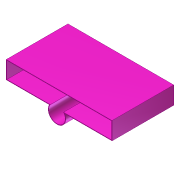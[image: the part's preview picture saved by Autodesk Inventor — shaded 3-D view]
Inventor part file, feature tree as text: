
AUTODESK INVENTOR PART (.ipt)
format: ipt  version: 2012 (Build 160160000, 160)  size: 87,552 bytes
history: native  units: in
note: dims shown in document units (in); Inventor stores cm internally (conversion verified against a paired STEP export)
features: extrude x1, shell x1, sketch x1
ambient origin geometry x8: Origin, YZ Plane, XZ Plane, XY Plane, X Axis, Y Axis, Z Axis, Center Point
bodies: Solid1 (feature_tree)
feature tree (3):
  extrude  "Extrusion1"  Depth=4.0in
  shell  "Shell1"  Thickness=8.0in
  sketch  "Sketch1"  dims[d0=14.0in d1=0.0in d2=4.0in d4=8.0in d5=2.0in d6=1.0in d7=0.125in d8=23.0in]
